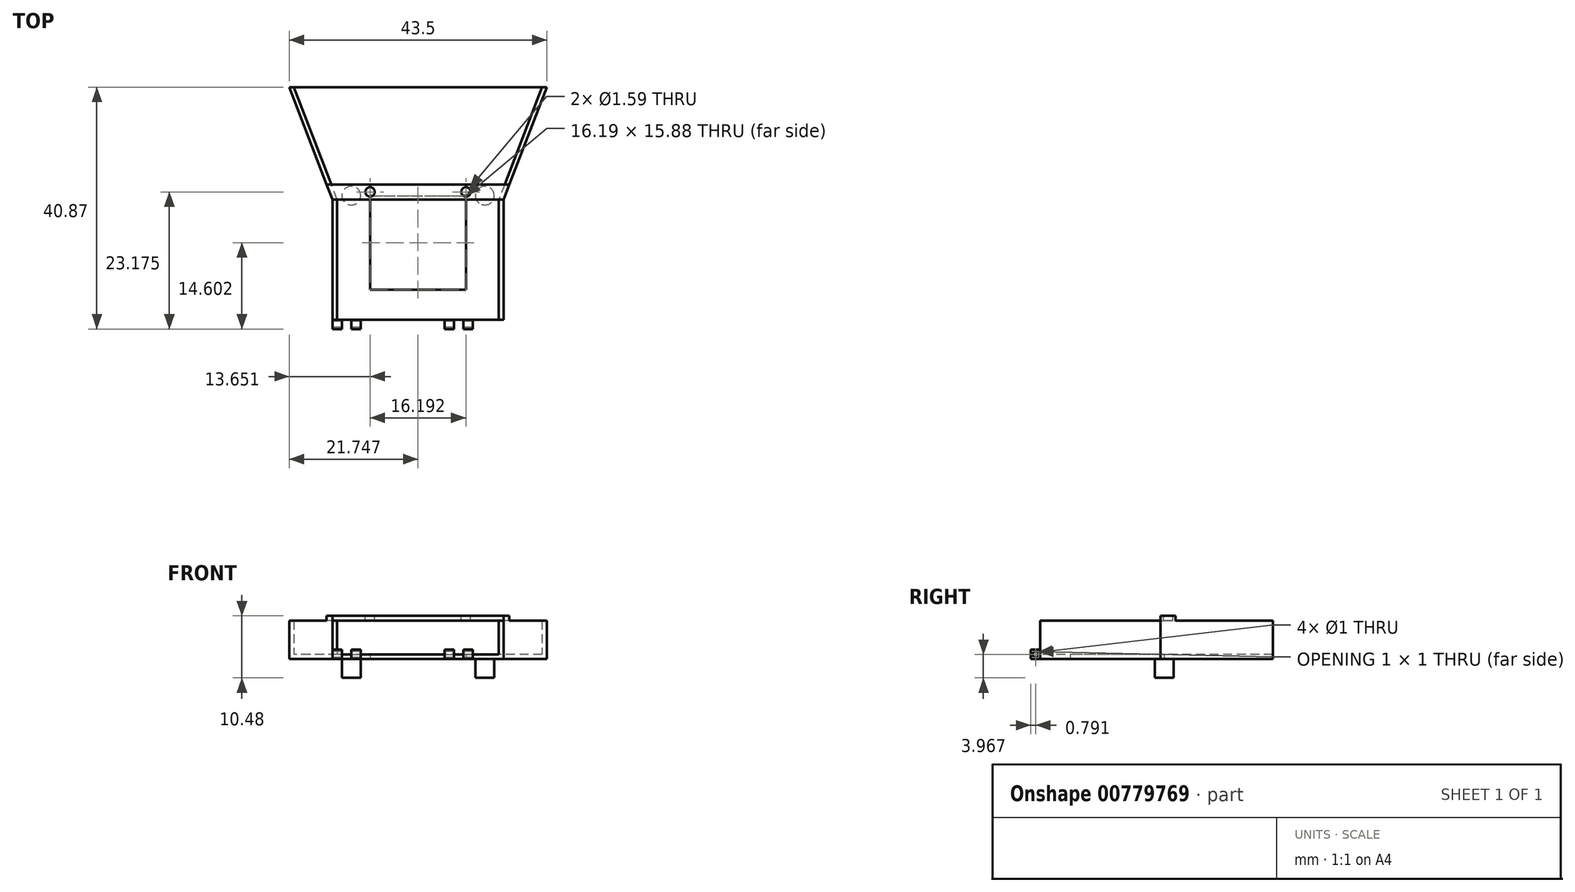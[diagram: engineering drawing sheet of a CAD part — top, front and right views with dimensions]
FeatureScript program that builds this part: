
annotation { "Feature Type Name" : "Feature", "Feature Type Description" : "" }
export const myFeature = defineFeature(function(context is Context, id is Id, definition is map)
    precondition{}
    {
        {
            var Q0;
            Q0=qCreatedBy(makeId("Top.planeOp"),FACE);
            var sketch = newSketch(context, id + "F0", { "sketchPlane" : qUnion([Q0])});
            skLineSegment(sketch, "E0", {"start": v(-18.37, 27.4) * mm, "end": v(-18.37, 7.09) * mm});
            skLineSegment(sketch, "E1", {"start": v(-18.37, 7.09) * mm, "end": v(10.52, 7.09) * mm});
            skLineSegment(sketch, "E2", {"start": v(10.52, 7.09) * mm, "end": v(10.52, 27.4) * mm});
            skLineSegment(sketch, "E3", {"start": v(10.52, 27.4) * mm, "end": v(17.83, 46.37) * mm});
            skLineSegment(sketch, "E4", {"start": v(17.83, 46.37) * mm, "end": v(-25.67, 46.37) * mm});
            skLineSegment(sketch, "E5", {"start": v(-25.67, 46.37) * mm, "end": v(-18.37, 27.4) * mm});
            skLineSegment(sketch, "E6.bottom", {"start": v(-12.02, 28.04) * mm, "end": v(4.17, 28.04) * mm});
            skLineSegment(sketch, "E6.top", {"start": v(-12.02, 12.17) * mm, "end": v(4.17, 12.17) * mm});
            skLineSegment(sketch, "E6.left", {"start": v(-12.02, 28.04) * mm, "end": v(-12.02, 12.17) * mm});
            skLineSegment(sketch, "E6.right", {"start": v(4.17, 28.04) * mm, "end": v(4.17, 12.17) * mm});
            skSolve(sketch);
        }
        {
            var Q0;
            Q0=makeQuery(id+"F0.imprint","IMPRINT",FACE,{"disambiguationData":[TD([[makeQuery(id+"F0.imprint","IMPRINT",EDGE,{"derivedFrom":sQuery(id+"F0.wireOp",EDGE,"E0")}),1.0]])]});
            extrude(context, id + "F1", {"entities" : qUnion([Q0]), "depth" : 0.32 * mm, "offsetDistance" : 25.4 * mm});
        }
        {
            var Q0;
            Q0=makeQuery(id+"F1.opExtrude","CAP_FACE",FACE,{"disambiguationData":[OSD([sQuery(id+"F0.wireOp",EDGE,"E0"),sQuery(id+"F0.wireOp",EDGE,"E1"),sQuery(id+"F0.wireOp",EDGE,"E2"),sQuery(id+"F0.wireOp",EDGE,"E3"),sQuery(id+"F0.wireOp",EDGE,"E4"),sQuery(id+"F0.wireOp",EDGE,"E5"),sQuery(id+"F0.wireOp",EDGE,"E6.bottom"),sQuery(id+"F0.wireOp",EDGE,"E6.top"),sQuery(id+"F0.wireOp",EDGE,"E6.left"),sQuery(id+"F0.wireOp",EDGE,"E6.right")])],"isStart":false});
            var sketch = newSketch(context, id + "F2", { "sketchPlane" : qUnion([Q0])});
            skLineSegment(sketch, "E7", {"start": v(-25.67, 46.37) * mm, "end": v(-18.37, 27.4) * mm});
            skLineSegment(sketch, "E8", {"start": v(-18.37, 27.4) * mm, "end": v(-18.37, 7.09) * mm});
            skLineSegment(sketch, "E9", {"start": v(-18.37, 7.09) * mm, "end": v(-17.58, 7.09) * mm});
            skLineSegment(sketch, "E10", {"start": v(-17.58, 7.09) * mm, "end": v(-17.58, 27.4) * mm});
            skLineSegment(sketch, "E11", {"start": v(-17.58, 27.4) * mm, "end": v(-24.88, 46.37) * mm});
            skLineSegment(sketch, "E12", {"start": v(-24.88, 46.37) * mm, "end": v(-25.67, 46.37) * mm});
            skLineSegment(sketch, "E13", {"start": v(10.52, 7.09) * mm, "end": v(10.52, 27.4) * mm});
            skLineSegment(sketch, "E14", {"start": v(10.52, 27.4) * mm, "end": v(17.83, 46.37) * mm});
            skLineSegment(sketch, "E15", {"start": v(17.83, 46.37) * mm, "end": v(17.03, 46.37) * mm});
            skLineSegment(sketch, "E16", {"start": v(17.03, 46.37) * mm, "end": v(9.73, 27.4) * mm});
            skLineSegment(sketch, "E17", {"start": v(9.73, 27.4) * mm, "end": v(9.73, 7.09) * mm});
            skLineSegment(sketch, "E18", {"start": v(9.73, 7.09) * mm, "end": v(10.52, 7.09) * mm});
            skSolve(sketch);
        }
        {
            var Q0;
            Q0=makeQuery(id+"F2.imprint","IMPRINT",FACE,{"disambiguationData":[TD([[makeQuery(id+"F2.imprint","IMPRINT",EDGE,{"derivedFrom":sQuery(id+"F2.wireOp",EDGE,"E13")}),1.0]])]});
            var Q1;
            Q1=makeQuery(id+"F2.imprint","IMPRINT",FACE,{"disambiguationData":[TD([[makeQuery(id+"F2.imprint","IMPRINT",EDGE,{"derivedFrom":sQuery(id+"F2.wireOp",EDGE,"E7")}),1.0]])]});
            extrude(context, id + "F3", {"entities" : qUnion([Q0, Q1]), "operationType" : NewBodyOperationType.ADD, "depth" : 5.7 * mm, "offsetDistance" : 25.4 * mm});
        }
        {
            var Q0;
            Q0=makeQuery(id+"F3.opExtrude","CAP_FACE",FACE,{"disambiguationData":[OSD([sQuery(id+"F2.wireOp",EDGE,"E7"),sQuery(id+"F2.wireOp",EDGE,"E8"),sQuery(id+"F2.wireOp",EDGE,"E9"),sQuery(id+"F2.wireOp",EDGE,"E10"),sQuery(id+"F2.wireOp",EDGE,"E11"),sQuery(id+"F2.wireOp",EDGE,"E12")])],"isStart":false});
            var sketch = newSketch(context, id + "F4", { "sketchPlane" : qUnion([Q0])});
            skLineSegment(sketch, "E19", {"start": v(-18.37, 27.4) * mm, "end": v(10.52, 27.4) * mm});
            skLineSegment(sketch, "E20", {"start": v(10.52, 27.4) * mm, "end": v(11.5, 29.95) * mm});
            skLineSegment(sketch, "E21", {"start": v(11.5, 29.95) * mm, "end": v(-19.35, 29.95) * mm});
            skLineSegment(sketch, "E22", {"start": v(-19.35, 29.95) * mm, "end": v(-18.37, 27.4) * mm});
            skSolve(sketch);
        }
        {
            var Q0;
            Q0 = qSketchRegion(id + "F4", true);
            extrude(context, id + "F5", {"entities" : qUnion([Q0]), "operationType" : NewBodyOperationType.ADD, "depth" : 0.8 * mm, "offsetDistance" : 25.4 * mm});
        }
        {
            var Q0;
            Q0=makeQuery(id+"F5.opExtrude","CAP_FACE",FACE,{"disambiguationData":[OSD([sQuery(id+"F4.wireOp",EDGE,"E19"),sQuery(id+"F4.wireOp",EDGE,"E20"),sQuery(id+"F4.wireOp",EDGE,"E21"),sQuery(id+"F4.wireOp",EDGE,"E22")])],"isStart":false});
            var sketch = newSketch(context, id + "F6", { "sketchPlane" : qUnion([Q0])});
            skCircle(sketch, "E23", {"center": v(-12.02, 28.68) * mm, "radius": 0.8 * mm});
            skCircle(sketch, "E24", {"center": v(4.17, 28.68) * mm, "radius": 0.8 * mm});
            skSolve(sketch);
        }
        {
            var Q0;
            Q0=makeQuery(id+"F6.imprint","IMPRINT",FACE,{"disambiguationData":[TD([[makeQuery(id+"F6.imprint","IMPRINT",EDGE,{"derivedFrom":sQuery(id+"F6.wireOp",EDGE,"E23")}),1.0]])]});
            var Q1;
            Q1=makeQuery(id+"F6.imprint","IMPRINT",FACE,{"disambiguationData":[TD([[makeQuery(id+"F6.imprint","IMPRINT",EDGE,{"derivedFrom":sQuery(id+"F6.wireOp",EDGE,"E24")}),1.0]])]});
            extrude(context, id + "F7", {"entities" : qUnion([Q0, Q1]), "operationType" : NewBodyOperationType.REMOVE, "oppositeDirection" : true, "depth" : 0.8 * mm, "offsetDistance" : 25.4 * mm});
        }
        {
            var Q0;
            Q0=makeQuery(id+"F1.opExtrude","CAP_FACE",FACE,{"disambiguationData":[OSD([sQuery(id+"F0.wireOp",EDGE,"E0"),sQuery(id+"F0.wireOp",EDGE,"E1"),sQuery(id+"F0.wireOp",EDGE,"E2"),sQuery(id+"F0.wireOp",EDGE,"E3"),sQuery(id+"F0.wireOp",EDGE,"E4"),sQuery(id+"F0.wireOp",EDGE,"E5"),sQuery(id+"F0.wireOp",EDGE,"E6.bottom"),sQuery(id+"F0.wireOp",EDGE,"E6.top"),sQuery(id+"F0.wireOp",EDGE,"E6.left"),sQuery(id+"F0.wireOp",EDGE,"E6.right")])],"isStart":true});
            extrude(context, id + "F8", {"entities" : qUnion([Q0]), "operationType" : NewBodyOperationType.ADD, "depth" : 0.32 * mm, "offsetDistance" : 25.4 * mm});
        }
        {
            var Q0;
            {var subQ0=sQuery(id+"F0.wireOp",EDGE,"E1");Q0=makeQuery(id+"F8.boolean.opBoolean","MERGE",FACE,{"derivedFrom":[makeQuery(id+"F3.boolean.opBoolean","MERGE",FACE,{"derivedFrom":[makeQuery(id+"F1.opExtrude","SWEPT_FACE",FACE,{"disambiguationData":[OSD([subQ0])]}),makeQuery(id+"F3.opExtrude","SWEPT_FACE",FACE,{"disambiguationData":[OSD([sQuery(id+"F2.wireOp",EDGE,"E9")])]}),makeQuery(id+"F3.opExtrude","SWEPT_FACE",FACE,{"disambiguationData":[OSD([sQuery(id+"F2.wireOp",EDGE,"E18")])]})]}),makeQuery(id+"F8.opExtrude","SWEPT_FACE",FACE,{"disambiguationData":[OSD([subQ0])]})]});}
            var sketch = newSketch(context, id + "F9", { "sketchPlane" : qUnion([Q0])});
            skLineSegment(sketch, "E25.bottom", {"start": v(-18.37, 0.32) * mm, "end": v(-16.78, 0.32) * mm});
            skLineSegment(sketch, "E25.top", {"start": v(-18.37, -0.32) * mm, "end": v(-16.78, -0.32) * mm});
            skLineSegment(sketch, "E25.left", {"start": v(-18.37, 0.32) * mm, "end": v(-18.37, -0.32) * mm});
            skLineSegment(sketch, "E25.right", {"start": v(-16.78, 0.32) * mm, "end": v(-16.78, -0.32) * mm});
            skLineSegment(sketch, "E26.bottom", {"start": v(-15.2, 0.32) * mm, "end": v(-13.6, 0.32) * mm});
            skLineSegment(sketch, "E26.top", {"start": v(-15.2, -0.32) * mm, "end": v(-13.6, -0.32) * mm});
            skLineSegment(sketch, "E26.left", {"start": v(-15.2, 0.32) * mm, "end": v(-15.2, -0.32) * mm});
            skLineSegment(sketch, "E26.right", {"start": v(-13.6, 0.32) * mm, "end": v(-13.6, -0.32) * mm});
            skLineSegment(sketch, "E27.bottom", {"start": v(5.35, 0.32) * mm, "end": v(3.76, 0.32) * mm});
            skLineSegment(sketch, "E27.top", {"start": v(5.35, -0.32) * mm, "end": v(3.76, -0.32) * mm});
            skLineSegment(sketch, "E27.left", {"start": v(5.35, 0.32) * mm, "end": v(5.35, -0.32) * mm});
            skLineSegment(sketch, "E27.right", {"start": v(3.76, 0.32) * mm, "end": v(3.76, -0.32) * mm});
            skLineSegment(sketch, "E28.bottom", {"start": v(2.17, 0.32) * mm, "end": v(0.59, 0.32) * mm});
            skLineSegment(sketch, "E28.top", {"start": v(2.17, -0.32) * mm, "end": v(0.59, -0.32) * mm});
            skLineSegment(sketch, "E28.left", {"start": v(2.17, 0.32) * mm, "end": v(2.17, -0.32) * mm});
            skLineSegment(sketch, "E28.right", {"start": v(0.59, 0.32) * mm, "end": v(0.59, -0.32) * mm});
            skSolve(sketch);
        }
        {
            var Q0;
            Q0=makeQuery(id+"F9.imprint","IMPRINT",FACE,{"disambiguationData":[TD([[makeQuery(id+"F9.imprint","IMPRINT",EDGE,{"derivedFrom":sQuery(id+"F9.wireOp",EDGE,"E25.bottom")}),-1.0]])]});
            var Q1;
            Q1=makeQuery(id+"F9.imprint","IMPRINT",FACE,{"disambiguationData":[TD([[makeQuery(id+"F9.imprint","IMPRINT",EDGE,{"derivedFrom":sQuery(id+"F9.wireOp",EDGE,"E26.bottom")}),-1.0]])]});
            var Q2;
            Q2=makeQuery(id+"F9.imprint","IMPRINT",FACE,{"disambiguationData":[TD([[makeQuery(id+"F9.imprint","IMPRINT",EDGE,{"derivedFrom":sQuery(id+"F9.wireOp",EDGE,"E28.bottom")}),-1.0]])]});
            var Q3;
            Q3=makeQuery(id+"F9.imprint","IMPRINT",FACE,{"disambiguationData":[TD([[makeQuery(id+"F9.imprint","IMPRINT",EDGE,{"derivedFrom":sQuery(id+"F9.wireOp",EDGE,"E27.bottom")}),-1.0]])]});
            extrude(context, id + "F10", {"entities" : qUnion([Q0, Q1, Q2, Q3]), "operationType" : NewBodyOperationType.ADD, "depth" : 1.59 * mm, "offsetDistance" : 25.4 * mm});
        }
        {
            var Q0;
            Q0=makeQuery(id+"F10.boolean.opBoolean","MERGE",FACE,{"derivedFrom":[makeQuery(id+"F8.opExtrude","CAP_FACE",FACE,{"disambiguationData":[OSD([sQuery(id+"F0.wireOp",EDGE,"E0"),sQuery(id+"F0.wireOp",EDGE,"E1"),sQuery(id+"F0.wireOp",EDGE,"E2"),sQuery(id+"F0.wireOp",EDGE,"E3"),sQuery(id+"F0.wireOp",EDGE,"E4"),sQuery(id+"F0.wireOp",EDGE,"E5"),sQuery(id+"F0.wireOp",EDGE,"E6.bottom"),sQuery(id+"F0.wireOp",EDGE,"E6.top"),sQuery(id+"F0.wireOp",EDGE,"E6.left"),sQuery(id+"F0.wireOp",EDGE,"E6.right")])],"isStart":false}),makeQuery(id+"F10.opExtrude","SWEPT_FACE",FACE,{"disambiguationData":[OSD([sQuery(id+"F9.wireOp",EDGE,"E25.top")])]}),makeQuery(id+"F10.opExtrude","SWEPT_FACE",FACE,{"disambiguationData":[OSD([sQuery(id+"F9.wireOp",EDGE,"E26.top")])]}),makeQuery(id+"F10.opExtrude","SWEPT_FACE",FACE,{"disambiguationData":[OSD([sQuery(id+"F9.wireOp",EDGE,"E27.top")])]}),makeQuery(id+"F10.opExtrude","SWEPT_FACE",FACE,{"disambiguationData":[OSD([sQuery(id+"F9.wireOp",EDGE,"E28.top")])]})]});
            extrude(context, id + "F11", {"entities" : qUnion([Q0]), "operationType" : NewBodyOperationType.ADD, "depth" : 0.32 * mm, "offsetDistance" : 25.4 * mm});
        }
        {
            var Q0;
            Q0=makeQuery(id+"F10.boolean.opBoolean","MERGE",FACE,{"derivedFrom":[makeQuery(id+"F1.opExtrude","CAP_FACE",FACE,{"disambiguationData":[OSD([sQuery(id+"F0.wireOp",EDGE,"E0"),sQuery(id+"F0.wireOp",EDGE,"E1"),sQuery(id+"F0.wireOp",EDGE,"E2"),sQuery(id+"F0.wireOp",EDGE,"E3"),sQuery(id+"F0.wireOp",EDGE,"E4"),sQuery(id+"F0.wireOp",EDGE,"E5"),sQuery(id+"F0.wireOp",EDGE,"E6.bottom"),sQuery(id+"F0.wireOp",EDGE,"E6.top"),sQuery(id+"F0.wireOp",EDGE,"E6.left"),sQuery(id+"F0.wireOp",EDGE,"E6.right")])],"isStart":false}),makeQuery(id+"F10.opExtrude","SWEPT_FACE",FACE,{"disambiguationData":[OSD([sQuery(id+"F9.wireOp",EDGE,"E25.bottom")])]}),makeQuery(id+"F10.opExtrude","SWEPT_FACE",FACE,{"disambiguationData":[OSD([sQuery(id+"F9.wireOp",EDGE,"E26.bottom")])]}),makeQuery(id+"F10.opExtrude","SWEPT_FACE",FACE,{"disambiguationData":[OSD([sQuery(id+"F9.wireOp",EDGE,"E27.bottom")])]}),makeQuery(id+"F10.opExtrude","SWEPT_FACE",FACE,{"disambiguationData":[OSD([sQuery(id+"F9.wireOp",EDGE,"E28.bottom")])]})]});
            var sketch = newSketch(context, id + "F12", { "sketchPlane" : qUnion([Q0])});
            skLineSegment(sketch, "E29.bottom", {"start": v(-16.78, 7.09) * mm, "end": v(-18.37, 7.09) * mm});
            skLineSegment(sketch, "E29.top", {"start": v(-16.78, 5.5) * mm, "end": v(-18.37, 5.5) * mm});
            skLineSegment(sketch, "E29.left", {"start": v(-16.78, 7.09) * mm, "end": v(-16.78, 5.5) * mm});
            skLineSegment(sketch, "E29.right", {"start": v(-18.37, 7.09) * mm, "end": v(-18.37, 5.5) * mm});
            skLineSegment(sketch, "E30.bottom", {"start": v(-15.2, 7.09) * mm, "end": v(-13.6, 7.09) * mm});
            skLineSegment(sketch, "E30.top", {"start": v(-15.2, 5.5) * mm, "end": v(-13.6, 5.5) * mm});
            skLineSegment(sketch, "E30.left", {"start": v(-15.2, 7.09) * mm, "end": v(-15.2, 5.5) * mm});
            skLineSegment(sketch, "E30.right", {"start": v(-13.6, 7.09) * mm, "end": v(-13.6, 5.5) * mm});
            skLineSegment(sketch, "E31.bottom", {"start": v(0.59, 7.09) * mm, "end": v(2.17, 7.09) * mm});
            skLineSegment(sketch, "E31.top", {"start": v(0.59, 5.5) * mm, "end": v(2.17, 5.5) * mm});
            skLineSegment(sketch, "E31.left", {"start": v(0.59, 7.09) * mm, "end": v(0.59, 5.5) * mm});
            skLineSegment(sketch, "E31.right", {"start": v(2.17, 7.09) * mm, "end": v(2.17, 5.5) * mm});
            skLineSegment(sketch, "E32.bottom", {"start": v(3.76, 7.09) * mm, "end": v(5.35, 7.09) * mm});
            skLineSegment(sketch, "E32.top", {"start": v(3.76, 5.5) * mm, "end": v(5.35, 5.5) * mm});
            skLineSegment(sketch, "E32.left", {"start": v(3.76, 7.09) * mm, "end": v(3.76, 5.5) * mm});
            skLineSegment(sketch, "E32.right", {"start": v(5.35, 7.09) * mm, "end": v(5.35, 5.5) * mm});
            skSolve(sketch);
        }
        {
            var Q0;
            Q0 = qSketchRegion(id + "F12", true);
            extrude(context, id + "F13", {"entities" : qUnion([Q0]), "operationType" : NewBodyOperationType.ADD, "depth" : 0.8 * mm, "offsetDistance" : 25.4 * mm});
        }
        {
            var Q0;
            Q0=makeQuery(id+"F11.opExtrude","CAP_FACE",FACE,{"disambiguationData":[OSD([sQuery(id+"F0.wireOp",EDGE,"E0"),sQuery(id+"F0.wireOp",EDGE,"E1"),sQuery(id+"F0.wireOp",EDGE,"E2"),sQuery(id+"F0.wireOp",EDGE,"E3"),sQuery(id+"F0.wireOp",EDGE,"E4"),sQuery(id+"F0.wireOp",EDGE,"E5"),sQuery(id+"F0.wireOp",EDGE,"E6.bottom"),sQuery(id+"F0.wireOp",EDGE,"E6.top"),sQuery(id+"F0.wireOp",EDGE,"E6.left"),sQuery(id+"F0.wireOp",EDGE,"E6.right"),sQuery(id+"F9.wireOp",EDGE,"E25.top"),sQuery(id+"F9.wireOp",EDGE,"E26.top"),sQuery(id+"F9.wireOp",EDGE,"E27.top"),sQuery(id+"F9.wireOp",EDGE,"E28.top")])],"isStart":false});
            extrude(context, id + "F14", {"entities" : qUnion([Q0]), "operationType" : NewBodyOperationType.REMOVE, "oppositeDirection" : true, "depth" : 0.16 * mm, "offsetDistance" : 25.4 * mm});
        }
        {
            var Q0;
            {var subQ0=sQuery(id+"F9.wireOp",EDGE,"E25.left");var subQ1=sQuery(id+"F0.wireOp",EDGE,"E0");Q0=makeQuery(id+"F13.boolean.opBoolean","MERGE",FACE,{"derivedFrom":[makeQuery(id+"F11.boolean.opBoolean","MERGE",FACE,{"derivedFrom":[makeQuery(id+"F10.boolean.opBoolean","MERGE",FACE,{"derivedFrom":[makeQuery(id+"F8.boolean.opBoolean","MERGE",FACE,{"derivedFrom":[makeQuery(id+"F3.boolean.opBoolean","MERGE",FACE,{"derivedFrom":[makeQuery(id+"F1.opExtrude","SWEPT_FACE",FACE,{"disambiguationData":[OSD([subQ1])]}),makeQuery(id+"F3.opExtrude","SWEPT_FACE",FACE,{"disambiguationData":[OSD([sQuery(id+"F2.wireOp",EDGE,"E8")])]})]}),makeQuery(id+"F8.opExtrude","SWEPT_FACE",FACE,{"disambiguationData":[OSD([subQ1])]})]}),makeQuery(id+"F10.opExtrude","SWEPT_FACE",FACE,{"disambiguationData":[OSD([subQ0])]})]}),makeQuery(id+"F11.opExtrude","SWEPT_FACE",FACE,{"disambiguationData":[OSD([subQ1,sQuery(id+"F9.wireOp",EDGE,"E25.top"),subQ0])]})]}),makeQuery(id+"F13.opExtrude","SWEPT_FACE",FACE,{"disambiguationData":[OSD([sQuery(id+"F12.wireOp",EDGE,"E29.right")])]})]});}
            var sketch = newSketch(context, id + "F15", { "sketchPlane" : qUnion([Q0])});
            skCircle(sketch, "E33", {"center": v(-6.3, 0.32) * mm, "radius": 0.5 * mm});
            skPoint(sketch, "E33.centerSnap0", {"position": v(-5.5, 0.32) * mm});
            skPoint(sketch, "E33.centerSnap1", {"position": v(-6.3, 1.11) * mm});
            skSolve(sketch);
        }
        {
            var Q0;
            Q0=makeQuery(id+"F15.imprint","IMPRINT",FACE,{"disambiguationData":[TD([[makeQuery(id+"F15.imprint","IMPRINT",EDGE,{"derivedFrom":sQuery(id+"F15.wireOp",EDGE,"E33")}),1.0]])]});
            extrude(context, id + "F16", {"entities" : qUnion([Q0]), "operationType" : NewBodyOperationType.REMOVE, "oppositeDirection" : true, "depth" : 25.4 * mm, "offsetDistance" : 25.4 * mm});
        }
        {
            var Q0;
            Q0=makeQuery(id+"F14.boolean.opBoolean","COPY",FACE,{"derivedFrom":makeQuery(id+"F14.opExtrude","CAP_FACE",FACE,{"disambiguationData":[OSD([sQuery(id+"F0.wireOp",EDGE,"E0"),sQuery(id+"F0.wireOp",EDGE,"E1"),sQuery(id+"F0.wireOp",EDGE,"E2"),sQuery(id+"F0.wireOp",EDGE,"E3"),sQuery(id+"F0.wireOp",EDGE,"E4"),sQuery(id+"F0.wireOp",EDGE,"E5"),sQuery(id+"F0.wireOp",EDGE,"E6.bottom"),sQuery(id+"F0.wireOp",EDGE,"E6.top"),sQuery(id+"F0.wireOp",EDGE,"E6.left"),sQuery(id+"F0.wireOp",EDGE,"E6.right"),sQuery(id+"F9.wireOp",EDGE,"E25.top"),sQuery(id+"F9.wireOp",EDGE,"E26.top"),sQuery(id+"F9.wireOp",EDGE,"E27.top"),sQuery(id+"F9.wireOp",EDGE,"E28.top")])],"isStart":false})});
            var sketch = newSketch(context, id + "F17", { "sketchPlane" : qUnion([Q0])});
            skCircle(sketch, "E34", {"center": v(-15.2, -28.04) * mm, "radius": 1.59 * mm});
            skCircle(sketch, "E35", {"center": v(7.35, -28.04) * mm, "radius": 1.59 * mm});
            skSolve(sketch);
        }
        {
            var Q0;
            Q0=makeQuery(id+"F17.imprint","IMPRINT",FACE,{"disambiguationData":[TD([[makeQuery(id+"F17.imprint","IMPRINT",EDGE,{"derivedFrom":sQuery(id+"F17.wireOp",EDGE,"E34")}),1.0]])]});
            var Q1;
            Q1=makeQuery(id+"F17.imprint","IMPRINT",FACE,{"disambiguationData":[TD([[makeQuery(id+"F17.imprint","IMPRINT",EDGE,{"derivedFrom":sQuery(id+"F17.wireOp",EDGE,"E35")}),1.0]])]});
            extrude(context, id + "F18", {"entities" : qUnion([Q0, Q1]), "operationType" : NewBodyOperationType.ADD, "depth" : 3.17 * mm, "offsetDistance" : 25.4 * mm});
        }
    });
